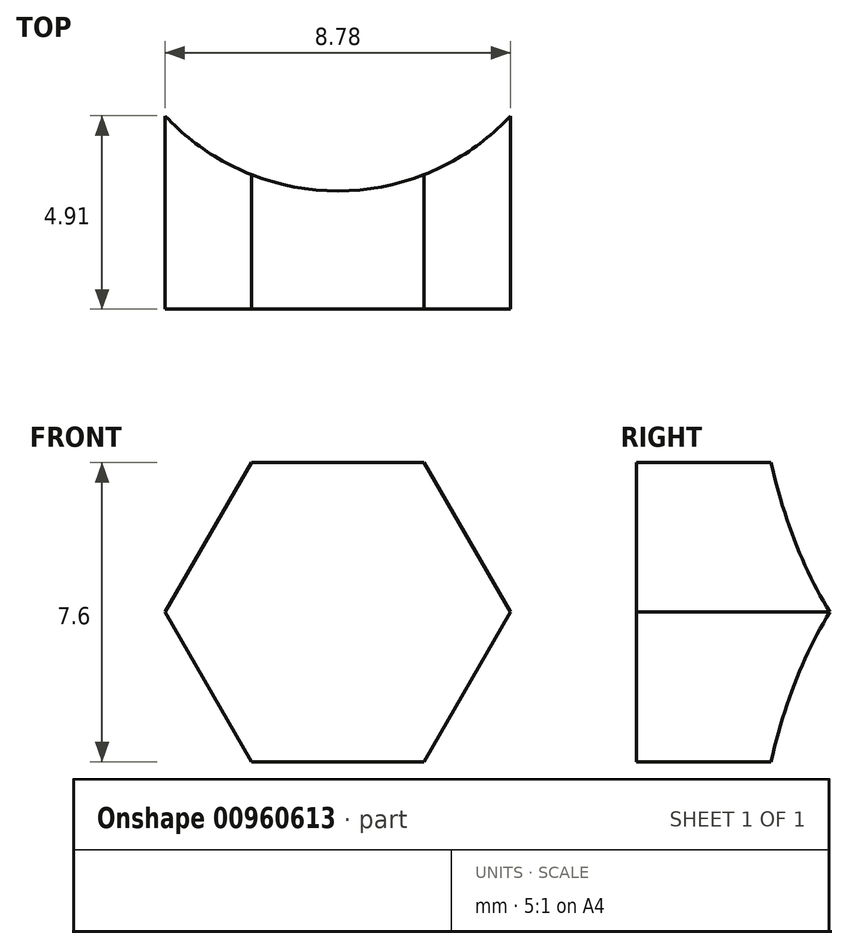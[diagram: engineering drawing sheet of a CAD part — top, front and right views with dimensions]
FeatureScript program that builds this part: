
annotation { "Feature Type Name" : "Feature", "Feature Type Description" : "" }
export const myFeature = defineFeature(function(context is Context, id is Id, definition is map)
    precondition{}
    {
        {
            var Q0;
            Q0=qCreatedBy(makeId("Front.planeOp"),FACE);
            var sketch = newSketch(context, id + "F0", { "sketchPlane" : qUnion([Q0])});
            skCircle(sketch, "E0.cCircle", {"center": v(0, 0) * mm, "radius": 3.8 * mm, "construction": true});
            skLineSegment(sketch, "E0.0", {"start": v(-2.2, 3.8) * mm, "end": v(2.2, 3.8) * mm});
            skLineSegment(sketch, "E0.1", {"start": v(2.2, 3.8) * mm, "end": v(4.39, 0) * mm});
            skLineSegment(sketch, "E0.2", {"start": v(4.39, 0) * mm, "end": v(2.2, -3.8) * mm});
            skLineSegment(sketch, "E0.3", {"start": v(2.2, -3.8) * mm, "end": v(-2.2, -3.8) * mm});
            skLineSegment(sketch, "E0.4", {"start": v(-2.2, -3.8) * mm, "end": v(-4.39, 0) * mm});
            skLineSegment(sketch, "E0.5", {"start": v(-4.39, 0) * mm, "end": v(-2.2, 3.8) * mm});
            skPoint(sketch, "E0.0.midPoint", {"position": v(0, 3.8) * mm});
            skSolve(sketch);
        }
        {
            var Q0;
            Q0=makeQuery(id+"F0.imprint","IMPRINT",FACE,{"disambiguationData":[TD([[makeQuery(id+"F0.imprint","IMPRINT",EDGE,{"derivedFrom":sQuery(id+"F0.wireOp",EDGE,"E0.0")}),-1.0]])]});
            extrude(context, id + "F1", {"entities" : qUnion([Q0]), "depth" : 9 * mm, "offsetDistance" : 25 * mm});
        }
        {
            var Q0;
            Q0=makeQuery(id+"F1.opExtrude","SWEPT_FACE",FACE,{"disambiguationData":[OSD([sQuery(id+"F0.wireOp",EDGE,"E0.0")])]});
            var sketch = newSketch(context, id + "F2", { "sketchPlane" : qUnion([Q0])});
            skCircle(sketch, "E1", {"center": v(0, 0) * mm, "radius": 6 * mm});
            skSolve(sketch);
        }
        {
            var Q0;
            {var subQ1=sQuery(id+"F0.wireOp",EDGE,"E0.0");var subQ6=makeQuery(id+"F1.opExtrude","CAP_EDGE",EDGE,{"disambiguationData":[OSD([subQ1])],"isStart":true});Q0=makeQuery(id+"F2.imprint","IMPRINT",FACE,{"disambiguationData":[TD([[makeQuery(id+"F2.imprint","IMPRINT",EDGE,{"derivedFrom":subQ6}),1.0]])]});}
            var Q1;
            {var subQ1=sQuery(id+"F0.wireOp",EDGE,"E0.0");var subQ6=makeQuery(id+"F1.opExtrude","CAP_EDGE",EDGE,{"disambiguationData":[OSD([subQ1])],"isStart":true});Q1=makeQuery(id+"F2.imprint","IMPRINT",FACE,{"disambiguationData":[TD([[makeQuery(id+"F2.imprint","IMPRINT",EDGE,{"derivedFrom":subQ6}),-1.0]])]});}
            extrude(context, id + "F3", {"entities" : qUnion([Q0, Q1]), "operationType" : NewBodyOperationType.REMOVE, "oppositeDirection" : true, "depth" : 25 * mm, "offsetDistance" : 25 * mm});
        }
    });
